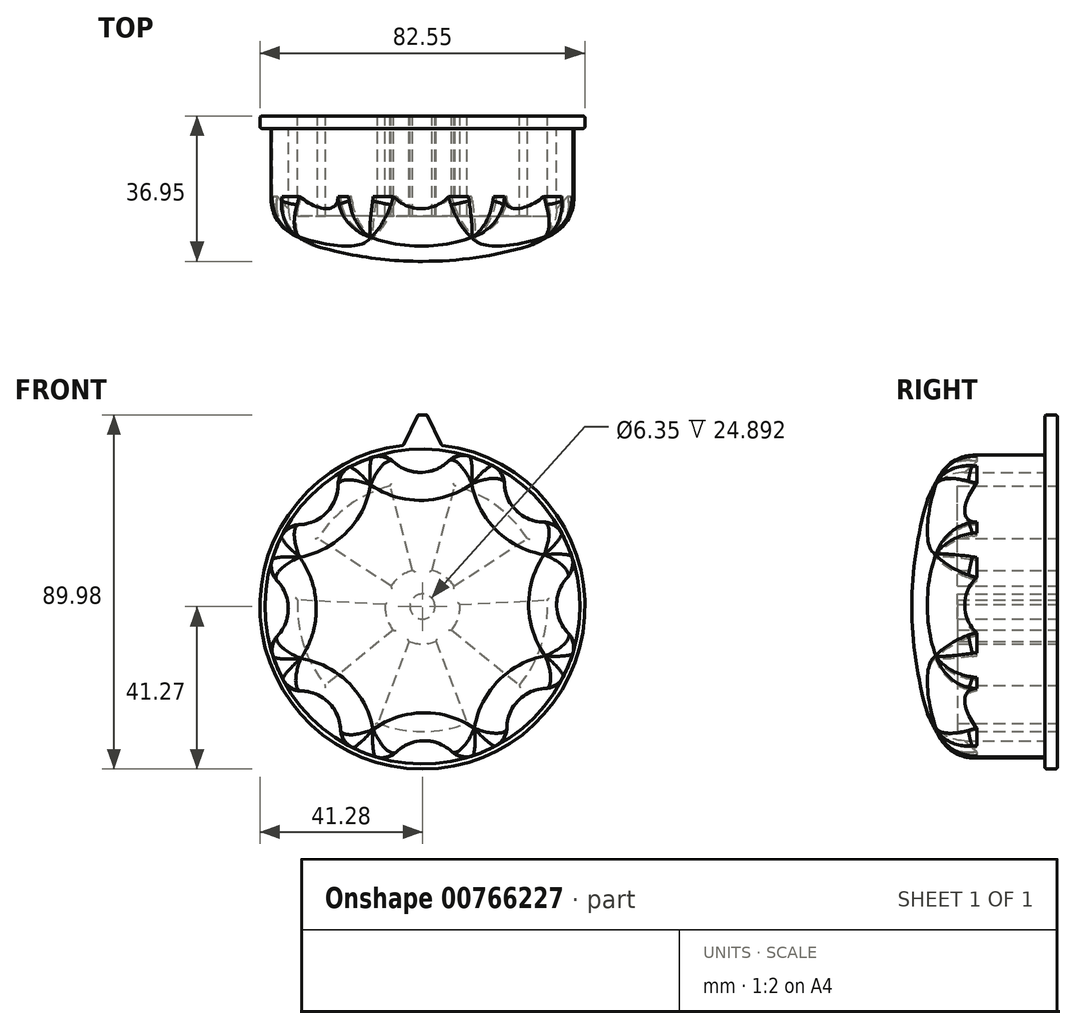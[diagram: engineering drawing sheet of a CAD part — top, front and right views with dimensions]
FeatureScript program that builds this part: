
annotation { "Feature Type Name" : "Feature", "Feature Type Description" : "" }
export const myFeature = defineFeature(function(context is Context, id is Id, definition is map)
    precondition{}
    {
        {
            var Q0;
            Q0=qCreatedBy(makeId("Front.planeOp"),FACE);
            var sketch = newSketch(context, id + "F0", { "sketchPlane" : qUnion([Q0])});
            skCircle(sketch, "E0", {"center": v(0, 0) * mm, "radius": 41.28 * mm});
            skLineSegment(sketch, "E1.bottom", {"start": v(1.17, 48.71) * mm, "end": v(-1.17, 48.71) * mm});
            skPoint(sketch, "E1.middle", {"position": v(0, 41.28) * mm});
            skLineSegment(sketch, "E2", {"start": v(1.17, 48.71) * mm, "end": v(4.83, 41) * mm});
            skLineSegment(sketch, "E3.MirrorCS", {"start": v(-1.17, 48.71) * mm, "end": v(-4.83, 41) * mm});
            skPoint(sketch, "E4.orphan", {"position": v(-4.7, 41.28) * mm});
            skPoint(sketch, "E5.orphan", {"position": v(4.7, 41.28) * mm});
            skPoint(sketch, "E6.orphan", {"position": v(4.7, 48.71) * mm});
            skPoint(sketch, "E7.orphan", {"position": v(-4.7, 48.71) * mm});
            skPoint(sketch, "E1.top.start.orphan", {"position": v(4.7, 33.84) * mm});
            skPoint(sketch, "E1.right.end.orphan", {"position": v(-4.7, 33.84) * mm});
            skCircle(sketch, "E8", {"center": v(0, 0) * mm, "radius": 40 * mm});
            skArc(sketch, "E9", {"start": v(-9.13, 38.95) * mm, "mid": v(-0.35, 34.08) * mm, "end": v(8.32, 39.13) * mm});
            skArc(sketch, "E10.1.0", {"start": v(-34, 21.09) * mm, "mid": v(-24.35, 23.85) * mm, "end": v(-21.78, 33.55) * mm});
            skArc(sketch, "E10.2.0", {"start": v(-38.95, -9.13) * mm, "mid": v(-34.08, -0.35) * mm, "end": v(-39.13, 8.32) * mm});
            skArc(sketch, "E11.2.3.0", {"start": v(-21.09, -34) * mm, "mid": v(-23.85, -24.35) * mm, "end": v(-33.55, -21.78) * mm});
            skArc(sketch, "E11.2.4.0", {"start": v(9.13, -38.95) * mm, "mid": v(0.35, -34.08) * mm, "end": v(-8.32, -39.13) * mm});
            skArc(sketch, "E11.2.5.0", {"start": v(34, -21.09) * mm, "mid": v(24.35, -23.85) * mm, "end": v(21.78, -33.55) * mm});
            skArc(sketch, "E11.2.6.0", {"start": v(38.95, 9.13) * mm, "mid": v(34.08, 0.35) * mm, "end": v(39.13, -8.32) * mm});
            skArc(sketch, "E11.2.7.0", {"start": v(21.09, 34) * mm, "mid": v(23.85, 24.35) * mm, "end": v(33.55, 21.78) * mm});
            skSolve(sketch);
        }
        {
            var Q0;
            {var subQ0=sQuery(id+"F0.wireOp",EDGE,"E9");Q0=makeQuery(id+"F0.imprint","IMPRINT",FACE,{"disambiguationData":[TD([[makeQuery(id+"F0.imprint","IMPRINT",EDGE,{"derivedFrom":subQ0}),-1.0]])]});}
            extrude(context, id + "F1", {"entities" : qUnion([Q0]), "depth" : 38.1 * mm, "offsetDistance" : 25.4 * mm});
        }
        {
            var Q0;
            {var subQ0=sQuery(id+"F0.wireOp",EDGE,"E11.2.7.0");Q0=makeQuery(id+"F0.imprint","IMPRINT",FACE,{"disambiguationData":[TD([[makeQuery(id+"F0.imprint","IMPRINT",EDGE,{"derivedFrom":subQ0}),1.0]])]});}
            var Q1;
            {var subQ0=sQuery(id+"F0.wireOp",EDGE,"E11.2.6.0");Q1=makeQuery(id+"F0.imprint","IMPRINT",FACE,{"disambiguationData":[TD([[makeQuery(id+"F0.imprint","IMPRINT",EDGE,{"derivedFrom":subQ0}),1.0]])]});}
            var Q2;
            {var subQ0=sQuery(id+"F0.wireOp",EDGE,"E11.2.5.0");Q2=makeQuery(id+"F0.imprint","IMPRINT",FACE,{"disambiguationData":[TD([[makeQuery(id+"F0.imprint","IMPRINT",EDGE,{"derivedFrom":subQ0}),1.0]])]});}
            var Q3;
            {var subQ0=sQuery(id+"F0.wireOp",EDGE,"E11.2.4.0");Q3=makeQuery(id+"F0.imprint","IMPRINT",FACE,{"disambiguationData":[TD([[makeQuery(id+"F0.imprint","IMPRINT",EDGE,{"derivedFrom":subQ0}),1.0]])]});}
            var Q4;
            {var subQ0=sQuery(id+"F0.wireOp",EDGE,"E11.2.3.0");Q4=makeQuery(id+"F0.imprint","IMPRINT",FACE,{"disambiguationData":[TD([[makeQuery(id+"F0.imprint","IMPRINT",EDGE,{"derivedFrom":subQ0}),1.0]])]});}
            var Q5;
            {var subQ0=sQuery(id+"F0.wireOp",EDGE,"E10.2.0");Q5=makeQuery(id+"F0.imprint","IMPRINT",FACE,{"disambiguationData":[TD([[makeQuery(id+"F0.imprint","IMPRINT",EDGE,{"derivedFrom":subQ0}),1.0]])]});}
            var Q6;
            {var subQ0=sQuery(id+"F0.wireOp",EDGE,"E10.1.0");Q6=makeQuery(id+"F0.imprint","IMPRINT",FACE,{"disambiguationData":[TD([[makeQuery(id+"F0.imprint","IMPRINT",EDGE,{"derivedFrom":subQ0}),1.0]])]});}
            var Q7;
            {var subQ0=sQuery(id+"F0.wireOp",EDGE,"E9");Q7=makeQuery(id+"F0.imprint","IMPRINT",FACE,{"disambiguationData":[TD([[makeQuery(id+"F0.imprint","IMPRINT",EDGE,{"derivedFrom":subQ0}),1.0]])]});}
            var Q8;
            {var subQ11=sQuery(id+"F0.wireOp",EDGE,"E0");var subQ12=makeQuery(id+"F0.imprint","INTERSECT",VERTEX,{"derivedFrom":[subQ11,sQuery(id+"F0.wireOp",EDGE,"E2")]});Q8=makeQuery(id+"F0.imprint","IMPRINT",FACE,{"disambiguationData":[TD([[makeQuery(id+"F0.imprint","IMPRINT",EDGE,{"disambiguationData":[TD([[subQ12,-1.0]])],"derivedFrom":subQ11}),1.0]])]});}
            var Q9;
            Q9=makeQuery(id+"F0.imprint","IMPRINT",FACE,{"disambiguationData":[TD([[makeQuery(id+"F0.imprint","IMPRINT",EDGE,{"derivedFrom":sQuery(id+"F0.wireOp",EDGE,"E1.bottom")}),1.0]])]});
            extrude(context, id + "F2", {"entities" : qUnion([Q0, Q1, Q2, Q3, Q4, Q5, Q6, Q7, Q8, Q9]), "operationType" : NewBodyOperationType.ADD, "depth" : 3.17 * mm, "offsetDistance" : 25.4 * mm});
        }
        {
            var Q0;
            {var subQ0=sQuery(id+"F0.wireOp",EDGE,"E9");var subQ1=sQuery(id+"F0.wireOp",EDGE,"E8");Q0=makeQuery(id+"F1.opExtrude","SWEPT_EDGE",EDGE,{"disambiguationData":[OSD([subQ1,subQ0]),TDD([makeQuery(id+"F0.imprint","INTERSECT",VERTEX,{"disambiguationData":[OD(1.0)],"derivedFrom":[subQ1,subQ0]})])]});}
            var Q1;
            {var subQ0=sQuery(id+"F0.wireOp",EDGE,"E9");var subQ1=sQuery(id+"F0.wireOp",EDGE,"E8");Q1=makeQuery(id+"F1.opExtrude","SWEPT_EDGE",EDGE,{"disambiguationData":[OSD([subQ1,subQ0]),TDD([makeQuery(id+"F0.imprint","INTERSECT",VERTEX,{"disambiguationData":[OD(0.0)],"derivedFrom":[subQ1,subQ0]})])]});}
            var Q2;
            {var subQ0=sQuery(id+"F0.wireOp",EDGE,"E10.1.0");var subQ1=sQuery(id+"F0.wireOp",EDGE,"E8");Q2=makeQuery(id+"F1.opExtrude","SWEPT_EDGE",EDGE,{"disambiguationData":[OSD([subQ1,subQ0]),TDD([makeQuery(id+"F0.imprint","INTERSECT",VERTEX,{"disambiguationData":[OD(1.0)],"derivedFrom":[subQ1,subQ0]})])]});}
            var Q3;
            {var subQ0=sQuery(id+"F0.wireOp",EDGE,"E10.1.0");var subQ1=sQuery(id+"F0.wireOp",EDGE,"E8");Q3=makeQuery(id+"F1.opExtrude","SWEPT_EDGE",EDGE,{"disambiguationData":[OSD([subQ1,subQ0]),TDD([makeQuery(id+"F0.imprint","INTERSECT",VERTEX,{"disambiguationData":[OD(0.0)],"derivedFrom":[subQ1,subQ0]})])]});}
            var Q4;
            {var subQ0=sQuery(id+"F0.wireOp",EDGE,"E10.2.0");var subQ1=sQuery(id+"F0.wireOp",EDGE,"E8");Q4=makeQuery(id+"F1.opExtrude","SWEPT_EDGE",EDGE,{"disambiguationData":[OSD([subQ1,subQ0]),TDD([makeQuery(id+"F0.imprint","INTERSECT",VERTEX,{"disambiguationData":[OD(1.0)],"derivedFrom":[subQ1,subQ0]})])]});}
            var Q5;
            {var subQ0=sQuery(id+"F0.wireOp",EDGE,"E10.2.0");var subQ1=sQuery(id+"F0.wireOp",EDGE,"E8");Q5=makeQuery(id+"F1.opExtrude","SWEPT_EDGE",EDGE,{"disambiguationData":[OSD([subQ1,subQ0]),TDD([makeQuery(id+"F0.imprint","INTERSECT",VERTEX,{"disambiguationData":[OD(0.0)],"derivedFrom":[subQ1,subQ0]})])]});}
            var Q6;
            {var subQ0=sQuery(id+"F0.wireOp",EDGE,"E11.2.3.0");var subQ1=sQuery(id+"F0.wireOp",EDGE,"E8");Q6=makeQuery(id+"F1.opExtrude","SWEPT_EDGE",EDGE,{"disambiguationData":[OSD([subQ1,subQ0]),TDD([makeQuery(id+"F0.imprint","INTERSECT",VERTEX,{"disambiguationData":[OD(1.0)],"derivedFrom":[subQ1,subQ0]})])]});}
            var Q7;
            {var subQ0=sQuery(id+"F0.wireOp",EDGE,"E11.2.3.0");var subQ1=sQuery(id+"F0.wireOp",EDGE,"E8");Q7=makeQuery(id+"F1.opExtrude","SWEPT_EDGE",EDGE,{"disambiguationData":[OSD([subQ1,subQ0]),TDD([makeQuery(id+"F0.imprint","INTERSECT",VERTEX,{"disambiguationData":[OD(0.0)],"derivedFrom":[subQ1,subQ0]})])]});}
            var Q8;
            {var subQ0=sQuery(id+"F0.wireOp",EDGE,"E11.2.4.0");var subQ1=sQuery(id+"F0.wireOp",EDGE,"E8");Q8=makeQuery(id+"F1.opExtrude","SWEPT_EDGE",EDGE,{"disambiguationData":[OSD([subQ1,subQ0]),TDD([makeQuery(id+"F0.imprint","INTERSECT",VERTEX,{"disambiguationData":[OD(1.0)],"derivedFrom":[subQ1,subQ0]})])]});}
            var Q9;
            {var subQ0=sQuery(id+"F0.wireOp",EDGE,"E11.2.4.0");var subQ1=sQuery(id+"F0.wireOp",EDGE,"E8");Q9=makeQuery(id+"F1.opExtrude","SWEPT_EDGE",EDGE,{"disambiguationData":[OSD([subQ1,subQ0]),TDD([makeQuery(id+"F0.imprint","INTERSECT",VERTEX,{"disambiguationData":[OD(0.0)],"derivedFrom":[subQ1,subQ0]})])]});}
            var Q10;
            {var subQ0=sQuery(id+"F0.wireOp",EDGE,"E11.2.5.0");var subQ1=sQuery(id+"F0.wireOp",EDGE,"E8");Q10=makeQuery(id+"F1.opExtrude","SWEPT_EDGE",EDGE,{"disambiguationData":[OSD([subQ1,subQ0]),TDD([makeQuery(id+"F0.imprint","INTERSECT",VERTEX,{"disambiguationData":[OD(1.0)],"derivedFrom":[subQ1,subQ0]})])]});}
            var Q11;
            {var subQ0=sQuery(id+"F0.wireOp",EDGE,"E11.2.5.0");var subQ1=sQuery(id+"F0.wireOp",EDGE,"E8");Q11=makeQuery(id+"F1.opExtrude","SWEPT_EDGE",EDGE,{"disambiguationData":[OSD([subQ1,subQ0]),TDD([makeQuery(id+"F0.imprint","INTERSECT",VERTEX,{"disambiguationData":[OD(0.0)],"derivedFrom":[subQ1,subQ0]})])]});}
            var Q12;
            {var subQ0=sQuery(id+"F0.wireOp",EDGE,"E11.2.6.0");var subQ1=sQuery(id+"F0.wireOp",EDGE,"E8");Q12=makeQuery(id+"F1.opExtrude","SWEPT_EDGE",EDGE,{"disambiguationData":[OSD([subQ1,subQ0]),TDD([makeQuery(id+"F0.imprint","INTERSECT",VERTEX,{"disambiguationData":[OD(1.0)],"derivedFrom":[subQ1,subQ0]})])]});}
            var Q13;
            {var subQ0=sQuery(id+"F0.wireOp",EDGE,"E11.2.6.0");var subQ1=sQuery(id+"F0.wireOp",EDGE,"E8");Q13=makeQuery(id+"F1.opExtrude","SWEPT_EDGE",EDGE,{"disambiguationData":[OSD([subQ1,subQ0]),TDD([makeQuery(id+"F0.imprint","INTERSECT",VERTEX,{"disambiguationData":[OD(0.0)],"derivedFrom":[subQ1,subQ0]})])]});}
            var Q14;
            {var subQ0=sQuery(id+"F0.wireOp",EDGE,"E11.2.7.0");var subQ1=sQuery(id+"F0.wireOp",EDGE,"E8");Q14=makeQuery(id+"F1.opExtrude","SWEPT_EDGE",EDGE,{"disambiguationData":[OSD([subQ1,subQ0]),TDD([makeQuery(id+"F0.imprint","INTERSECT",VERTEX,{"disambiguationData":[OD(1.0)],"derivedFrom":[subQ1,subQ0]})])]});}
            var Q15;
            {var subQ0=sQuery(id+"F0.wireOp",EDGE,"E11.2.7.0");var subQ1=sQuery(id+"F0.wireOp",EDGE,"E8");Q15=makeQuery(id+"F1.opExtrude","SWEPT_EDGE",EDGE,{"disambiguationData":[OSD([subQ1,subQ0]),TDD([makeQuery(id+"F0.imprint","INTERSECT",VERTEX,{"disambiguationData":[OD(0.0)],"derivedFrom":[subQ1,subQ0]})])]});}
            fillet(context, id + "F3", {"entities" : qUnion([Q0, Q1, Q2, Q3, Q4, Q5, Q6, Q7, Q8, Q9, Q10, Q11, Q12, Q13, Q14, Q15]), "radius" : 5.08 * mm, "tangentPropagation" : true, "allowEdgeOverflow" : false});
        }
        {
            var Q0;
            Q0=qCreatedBy(makeId("Top.planeOp"),FACE);
            var sketch = newSketch(context, id + "F4", { "sketchPlane" : qUnion([Q0])});
            skLineSegment(sketch, "E12", {"start": v(0, -48.72) * mm, "end": v(0, 11.42) * mm});
            skArc(sketch, "E13", {"start": v(0, -36.95) * mm, "mid": v(33.99, -30.68) * mm, "end": v(63.5, -12.7) * mm});
            skPoint(sketch, "E14.orphan", {"position": v(-63.5, -12.7) * mm});
            skLineSegment(sketch, "E15", {"start": v(63.5, -12.7) * mm, "end": v(63.5, -48.72) * mm});
            skLineSegment(sketch, "E16", {"start": v(63.5, -48.72) * mm, "end": v(0, -48.72) * mm});
            skPoint(sketch, "E17.orphan", {"position": v(0, -51.78) * mm});
            skSolve(sketch);
        }
        {
            var Q0;
            Q0 = qSketchRegion(id + "F4", true);
            var Q1;
            Q1=sQuery(id+"F4.wireOp",EDGE,"E12");
            revolve(context, id + "F5", {"operationType" : NewBodyOperationType.REMOVE, "surfaceOperationType" : NewSurfaceOperationType.NEW, "entities" : qUnion([Q0]), "axis" : qUnion([Q1]), "revolveType" : RevolveType.FULL, "oppositeDirection" : true});
        }
        {
            var Q0;
            Q0=makeQuery(id+"F5.boolean.opBoolean","COPY",FACE,{"derivedFrom":makeQuery(id+"F5.opRevolve","SWEPT_FACE",FACE,{"disambiguationData":[OSD([sQuery(id+"F4.wireOp",EDGE,"E13")])]})});
            fillet(context, id + "F6", {"entities" : qUnion([Q0]), "radius" : 9.9 * mm, "tangentPropagation" : true, "allowEdgeOverflow" : false});
        }
        {
            var Q0;
            Q0=qCreatedBy(makeId("Front.planeOp"),FACE);
            var sketch = newSketch(context, id + "F7", { "sketchPlane" : qUnion([Q0])});
            skCircle(sketch, "E18", {"center": v(0, 0) * mm, "radius": 3.18 * mm});
            skCircle(sketch, "E19", {"center": v(0, 0) * mm, "radius": 9.53 * mm});
            skCircle(sketch, "E20", {"center": v(0, 0) * mm, "radius": 31.75 * mm});
            skLineSegment(sketch, "E21.trimOffspring", {"start": v(-2.47, 9.2) * mm, "end": v(-8.22, 30.67) * mm});
            skLineSegment(sketch, "E22.MirrorCS", {"start": v(2.47, 9.2) * mm, "end": v(8.22, 30.67) * mm});
            skLineSegment(sketch, "E23.1.0", {"start": v(-7.99, 5.19) * mm, "end": v(-26.63, 17.3) * mm});
            skLineSegment(sketch, "E23.1.1", {"start": v(-9.51, 0.5) * mm, "end": v(-31.7, 1.66) * mm});
            skLineSegment(sketch, "E23.2.0", {"start": v(-7.4, -6) * mm, "end": v(-24.67, -19.98) * mm});
            skLineSegment(sketch, "E23.2.1", {"start": v(-3.41, -8.9) * mm, "end": v(-11.38, -29.64) * mm});
            skLineSegment(sketch, "E24.1.3.0", {"start": v(3.41, -8.9) * mm, "end": v(11.38, -29.64) * mm});
            skLineSegment(sketch, "E24.3.3.0", {"start": v(7.4, -6) * mm, "end": v(24.67, -19.98) * mm});
            skLineSegment(sketch, "E24.1.4.0", {"start": v(9.51, 0.5) * mm, "end": v(31.7, 1.66) * mm});
            skLineSegment(sketch, "E24.3.4.0", {"start": v(7.99, 5.19) * mm, "end": v(26.63, 17.3) * mm});
            skSolve(sketch);
        }
        {
            var Q0;
            {var subQ0=sQuery(id+"F7.wireOp",EDGE,"E22.MirrorCS");Q0=makeQuery(id+"F7.imprint","IMPRINT",FACE,{"disambiguationData":[TD([[makeQuery(id+"F7.imprint","IMPRINT",EDGE,{"derivedFrom":subQ0}),-1.0]])]});}
            var Q1;
            {var subQ0=sQuery(id+"F7.wireOp",EDGE,"E21.trimOffspring");Q1=makeQuery(id+"F7.imprint","IMPRINT",FACE,{"disambiguationData":[TD([[makeQuery(id+"F7.imprint","IMPRINT",EDGE,{"derivedFrom":subQ0}),1.0]])]});}
            var Q2;
            {var subQ0=sQuery(id+"F7.wireOp",EDGE,"E23.1.1");Q2=makeQuery(id+"F7.imprint","IMPRINT",FACE,{"disambiguationData":[TD([[makeQuery(id+"F7.imprint","IMPRINT",EDGE,{"derivedFrom":subQ0}),1.0]])]});}
            var Q3;
            {var subQ0=sQuery(id+"F7.wireOp",EDGE,"E23.2.1");Q3=makeQuery(id+"F7.imprint","IMPRINT",FACE,{"disambiguationData":[TD([[makeQuery(id+"F7.imprint","IMPRINT",EDGE,{"derivedFrom":subQ0}),1.0]])]});}
            var Q4;
            {var subQ0=sQuery(id+"F7.wireOp",EDGE,"E24.3.3.0");Q4=makeQuery(id+"F7.imprint","IMPRINT",FACE,{"disambiguationData":[TD([[makeQuery(id+"F7.imprint","IMPRINT",EDGE,{"derivedFrom":subQ0}),1.0]])]});}
            var Q5;
            Q5=makeQuery(id+"F7.imprint","IMPRINT",FACE,{"disambiguationData":[TD([[makeQuery(id+"F7.imprint","IMPRINT",EDGE,{"derivedFrom":sQuery(id+"F7.wireOp",EDGE,"E18")}),1.0]])]});
            extrude(context, id + "F8", {"entities" : qUnion([Q0, Q1, Q2, Q3, Q4, Q5]), "operationType" : NewBodyOperationType.REMOVE, "depth" : 25.4 * mm, "offsetDistance" : 25.4 * mm});
        }
        {
            var Q0;
            Q0=makeQuery(id+"F2.opExtrude","CAP_EDGE",EDGE,{"disambiguationData":[OSD([sQuery(id+"F0.wireOp",EDGE,"E0")])],"isStart":true});
            var Q1;
            Q1=makeQuery(id+"F2.opExtrude","CAP_EDGE",EDGE,{"disambiguationData":[OSD([sQuery(id+"F0.wireOp",EDGE,"E0")])],"isStart":false});
            var Q2;
            Q2=makeQuery(id+"F2.opExtrude","CAP_EDGE",EDGE,{"disambiguationData":[OSD([sQuery(id+"F0.wireOp",EDGE,"E3.MirrorCS")])],"isStart":true});
            var Q3;
            Q3=makeQuery(id+"F2.opExtrude","CAP_EDGE",EDGE,{"disambiguationData":[OSD([sQuery(id+"F0.wireOp",EDGE,"E1.bottom")])],"isStart":true});
            var Q4;
            Q4=makeQuery(id+"F2.opExtrude","CAP_EDGE",EDGE,{"disambiguationData":[OSD([sQuery(id+"F0.wireOp",EDGE,"E2")])],"isStart":true});
            var Q5;
            Q5=makeQuery(id+"F2.opExtrude","SWEPT_EDGE",EDGE,{"disambiguationData":[OSD([sQuery(id+"F0.wireOp",EDGE,"E1.bottom"),sQuery(id+"F0.wireOp",EDGE,"E3.MirrorCS")])]});
            var Q6;
            Q6=makeQuery(id+"F2.opExtrude","SWEPT_FACE",FACE,{"disambiguationData":[OSD([sQuery(id+"F0.wireOp",EDGE,"E3.MirrorCS")])]});
            var Q7;
            Q7=makeQuery(id+"F2.opExtrude","SWEPT_FACE",FACE,{"disambiguationData":[OSD([sQuery(id+"F0.wireOp",EDGE,"E2")])]});
            var Q8;
            Q8=makeQuery(id+"F2.opExtrude","CAP_FACE",FACE,{"disambiguationData":[OSD([sQuery(id+"F0.wireOp",EDGE,"E0"),sQuery(id+"F0.wireOp",EDGE,"E1.bottom"),sQuery(id+"F0.wireOp",EDGE,"E2"),sQuery(id+"F0.wireOp",EDGE,"E3.MirrorCS"),sQuery(id+"F0.wireOp",EDGE,"E8"),sQuery(id+"F0.wireOp",EDGE,"E9"),sQuery(id+"F0.wireOp",EDGE,"E10.1.0"),sQuery(id+"F0.wireOp",EDGE,"E10.2.0"),sQuery(id+"F0.wireOp",EDGE,"E11.2.3.0"),sQuery(id+"F0.wireOp",EDGE,"E11.2.4.0"),sQuery(id+"F0.wireOp",EDGE,"E11.2.5.0"),sQuery(id+"F0.wireOp",EDGE,"E11.2.6.0"),sQuery(id+"F0.wireOp",EDGE,"E11.2.7.0")])],"isStart":false});
            var Q9;
            {var subQ0=sQuery(id+"F0.wireOp",EDGE,"E11.2.7.0");var subQ1=sQuery(id+"F0.wireOp",EDGE,"E11.2.6.0");var subQ2=sQuery(id+"F0.wireOp",EDGE,"E11.2.5.0");var subQ3=sQuery(id+"F0.wireOp",EDGE,"E11.2.4.0");var subQ4=sQuery(id+"F0.wireOp",EDGE,"E11.2.3.0");var subQ5=sQuery(id+"F0.wireOp",EDGE,"E10.2.0");var subQ6=sQuery(id+"F0.wireOp",EDGE,"E10.1.0");var subQ7=sQuery(id+"F0.wireOp",EDGE,"E9");var subQ8=sQuery(id+"F0.wireOp",EDGE,"E8");Q9=makeQuery(id+"F2.boolean.opBoolean","MERGE",FACE,{"derivedFrom":[makeQuery(id+"F1.opExtrude","CAP_FACE",FACE,{"disambiguationData":[OSD([subQ8,subQ7,subQ6,subQ5,subQ4,subQ3,subQ2,subQ1,subQ0])],"isStart":true}),makeQuery(id+"F2.opExtrude","CAP_FACE",FACE,{"disambiguationData":[OSD([sQuery(id+"F0.wireOp",EDGE,"E0"),sQuery(id+"F0.wireOp",EDGE,"E1.bottom"),sQuery(id+"F0.wireOp",EDGE,"E2"),sQuery(id+"F0.wireOp",EDGE,"E3.MirrorCS"),subQ8,subQ7,subQ6,subQ5,subQ4,subQ3,subQ2,subQ1,subQ0])],"isStart":true})]});}
            fillet(context, id + "F9", {"entities" : qUnion([Q0, Q1, Q2, Q3, Q4, Q5, Q6, Q7, Q8, Q9]), "radius" : 0.5 * mm, "tangentPropagation" : true, "allowEdgeOverflow" : false});
        }
    });
